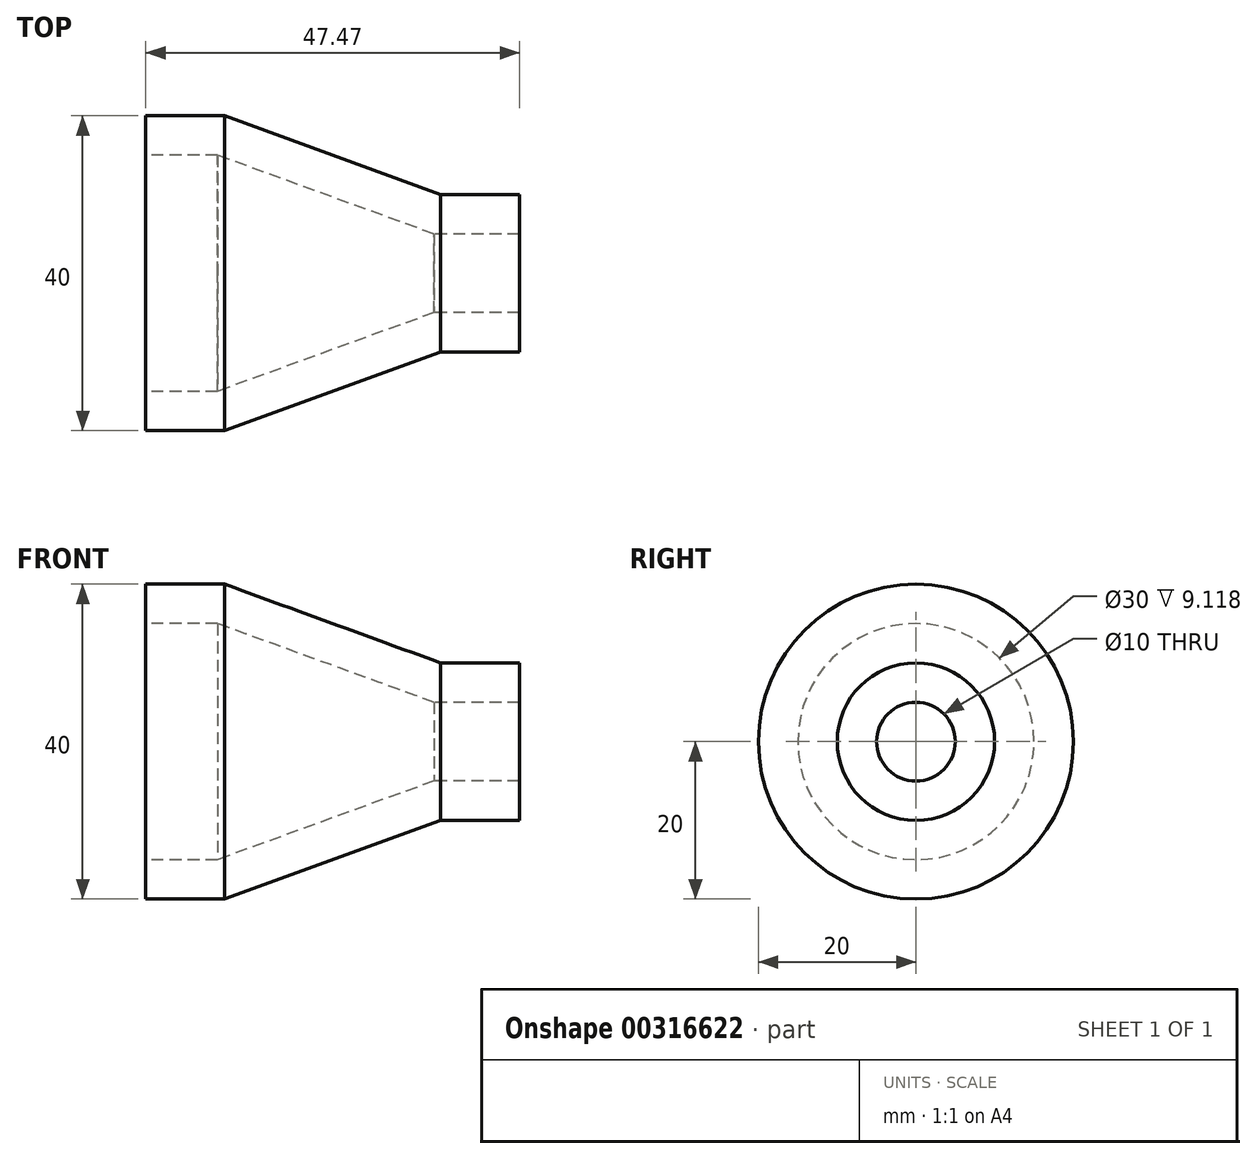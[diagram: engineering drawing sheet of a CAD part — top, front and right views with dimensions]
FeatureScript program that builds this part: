
annotation { "Feature Type Name" : "Feature", "Feature Type Description" : "" }
export const myFeature = defineFeature(function(context is Context, id is Id, definition is map)
    precondition{}
    {
        {
            var Q0;
            Q0=qCreatedBy(makeId("Front.planeOp"),FACE);
            var sketch = newSketch(context, id + "F0", { "sketchPlane" : qUnion([Q0])});
            skLineSegment(sketch, "E0", {"start": v(0, 0) * mm, "end": v(0, 15) * mm});
            skLineSegment(sketch, "E1", {"start": v(0, 15) * mm, "end": v(0, 20) * mm});
            skLineSegment(sketch, "E2", {"start": v(0, 20) * mm, "end": v(10, 20) * mm});
            skLineSegment(sketch, "E3", {"start": v(10, 20) * mm, "end": v(37.47, 10) * mm});
            skLineSegment(sketch, "E4", {"start": v(37.47, 10) * mm, "end": v(47.47, 10) * mm});
            skLineSegment(sketch, "E5", {"start": v(47.47, 10) * mm, "end": v(47.47, 5) * mm});
            skLineSegment(sketch, "E6", {"start": v(47.47, 5) * mm, "end": v(36.6, 5) * mm});
            skLineSegment(sketch, "E7", {"start": v(36.6, 5) * mm, "end": v(9.12, 15) * mm});
            skLineSegment(sketch, "E8", {"start": v(9.12, 15) * mm, "end": v(0, 15) * mm});
            skLineSegment(sketch, "E9", {"start": v(47.47, 5) * mm, "end": v(47.47, 0) * mm});
            skLineSegment(sketch, "E10", {"start": v(0, 0) * mm, "end": v(47.47, 0) * mm});
            skSolve(sketch);
        }
        {
            var Q0;
            Q0=makeQuery(id+"F0.imprint","IMPRINT",FACE,{"disambiguationData":[TD([[makeQuery(id+"F0.imprint","IMPRINT",EDGE,{"derivedFrom":sQuery(id+"F0.wireOp",EDGE,"E1")}),-1.0]])]});
            var Q1;
            Q1=sQuery(id+"F0.wireOp",EDGE,"E10");
            revolve(context, id + "F1", {"entities" : qUnion([Q0]), "axis" : qUnion([Q1]), "revolveType" : RevolveType.FULL});
        }
        {
            var Q0;
            Q0=makeQuery(id+"F0.imprint","IMPRINT",FACE,{"disambiguationData":[TD([[makeQuery(id+"F0.imprint","IMPRINT",EDGE,{"derivedFrom":sQuery(id+"F0.wireOp",EDGE,"E0")}),-1.0]])]});
            var Q1;
            Q1=sQuery(id+"F0.wireOp",EDGE,"E10");
            revolve(context, id + "F2", {"entities" : qUnion([Q0]), "axis" : qUnion([Q1]), "revolveType" : RevolveType.FULL});
        }
    });
